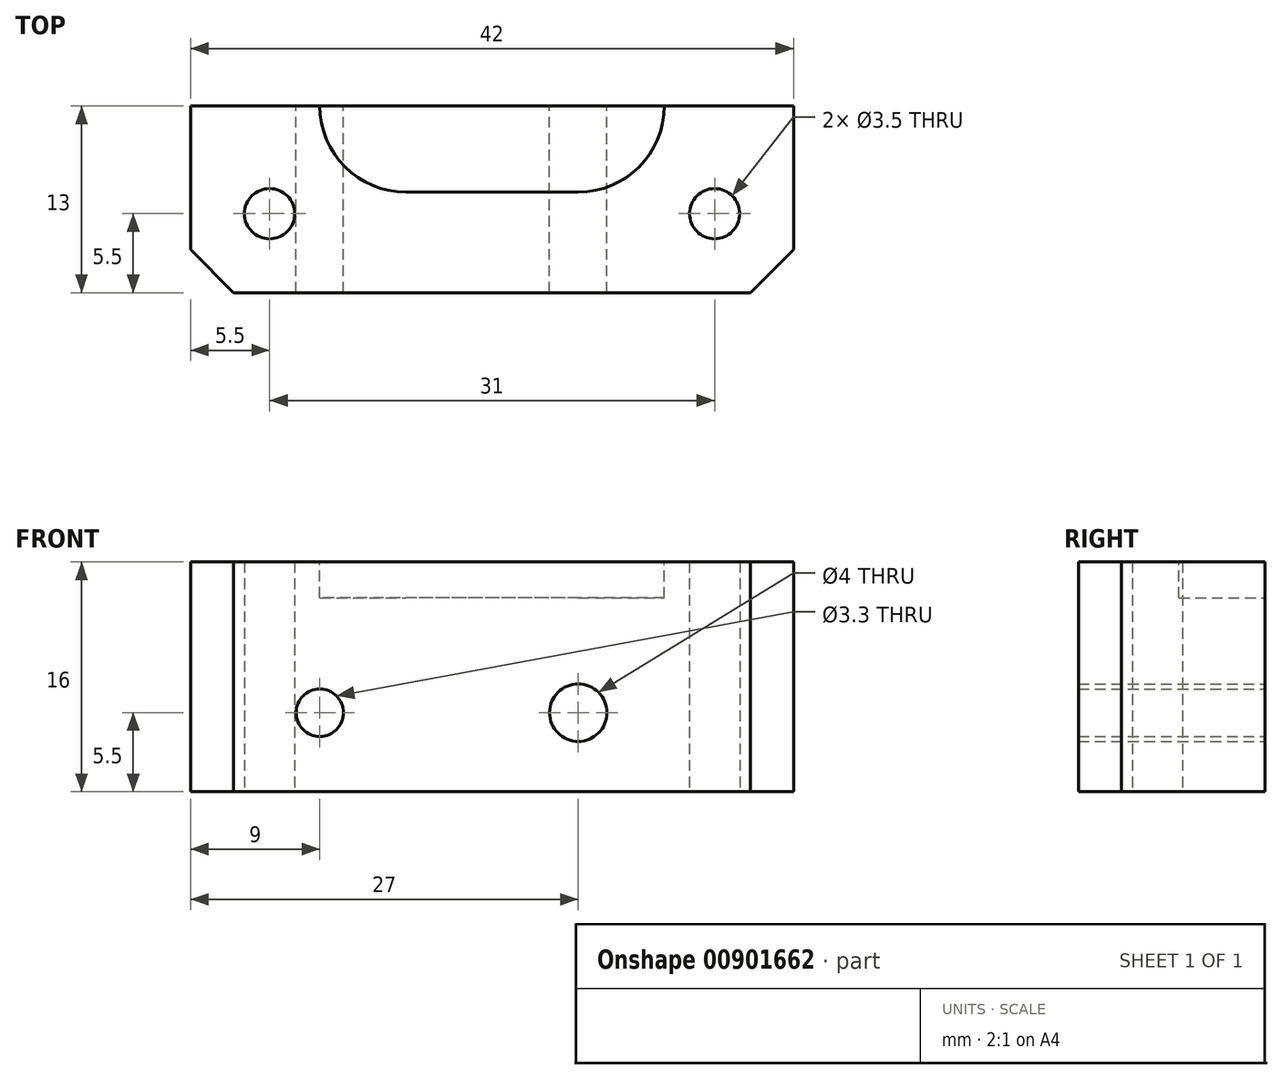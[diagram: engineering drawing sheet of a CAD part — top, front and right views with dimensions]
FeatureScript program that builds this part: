
annotation { "Feature Type Name" : "Feature", "Feature Type Description" : "" }
export const myFeature = defineFeature(function(context is Context, id is Id, definition is map)
    precondition{}
    {
        {
            var Q0;
            Q0=qCreatedBy(makeId("Top.planeOp"),FACE);
            var sketch = newSketch(context, id + "F0", { "sketchPlane" : qUnion([Q0])});
            skLineSegment(sketch, "E0.bottom", {"start": v(21, 6.5) * mm, "end": v(-21, 6.5) * mm});
            skLineSegment(sketch, "E0.top", {"start": v(21, -6.5) * mm, "end": v(-21, -6.5) * mm});
            skLineSegment(sketch, "E0.left", {"start": v(21, 6.5) * mm, "end": v(21, -6.5) * mm});
            skLineSegment(sketch, "E0.right", {"start": v(-21, 6.5) * mm, "end": v(-21, -6.5) * mm});
            skPoint(sketch, "E0.middle", {"position": v(0, 0) * mm});
            skCircle(sketch, "E1", {"center": v(-15.5, -1) * mm, "radius": 1.75 * mm});
            skLineSegment(sketch, "E2", {"start": v(0, 8.77) * mm, "end": v(0, -9.46) * mm, "construction": true});
            skPoint(sketch, "E2.endSnap0", {"position": v(0, 6.5) * mm});
            skCircle(sketch, "E3.MirrorC", {"center": v(15.5, -1) * mm, "radius": 1.75 * mm});
            skSolve(sketch);
        }
        {
            var Q0;
            Q0 = qSketchRegion(id + "F0", true);
            extrude(context, id + "F1", {"entities" : qUnion([Q0]), "endBound" : BoundingType.SYMMETRIC, "depth" : 16 * mm, "offsetDistance" : 25 * mm});
        }
        {
            var Q0;
            Q0=makeQuery(id+"F1.opExtrude","CAP_FACE",FACE,{"disambiguationData":[OSD([sQuery(id+"F0.wireOp",EDGE,"E0.bottom"),sQuery(id+"F0.wireOp",EDGE,"E0.top"),sQuery(id+"F0.wireOp",EDGE,"E0.left"),sQuery(id+"F0.wireOp",EDGE,"E0.right"),sQuery(id+"F0.wireOp",EDGE,"E1"),sQuery(id+"F0.wireOp",EDGE,"E3.MirrorC")])],"isStart":false});
            var sketch = newSketch(context, id + "F2", { "sketchPlane" : qUnion([Q0])});
            skLineSegment(sketch, "E4", {"start": v(0, 9.79) * mm, "end": v(0, -9.6) * mm, "construction": true});
            skLineSegment(sketch, "E5.bottom", {"start": v(12, 6.5) * mm, "end": v(-12, 6.5) * mm});
            skLineSegment(sketch, "E5.top", {"start": v(12, 0.5) * mm, "end": v(-12, 0.5) * mm});
            skLineSegment(sketch, "E5.left", {"start": v(12, 6.5) * mm, "end": v(12, 0.5) * mm});
            skLineSegment(sketch, "E5.right", {"start": v(-12, 6.5) * mm, "end": v(-12, 0.5) * mm});
            skPoint(sketch, "E5.middle", {"position": v(0, 3.5) * mm});
            skSolve(sketch);
        }
        {
            var Q0;
            Q0 = qSketchRegion(id + "F2", true);
            extrude(context, id + "F3", {"entities" : qUnion([Q0]), "operationType" : NewBodyOperationType.REMOVE, "oppositeDirection" : true, "depth" : 2.5 * mm, "offsetDistance" : 25 * mm});
        }
        {
            var Q0;
            Q0=makeQuery(id+"F3.boolean.opBoolean","COPY",EDGE,{"derivedFrom":makeQuery(id+"F3.opExtrude","SWEPT_EDGE",EDGE,{"disambiguationData":[OSD([sQuery(id+"F2.wireOp",EDGE,"E5.top"),sQuery(id+"F2.wireOp",EDGE,"E5.right")])]})});
            var Q1;
            Q1=makeQuery(id+"F3.boolean.opBoolean","COPY",EDGE,{"derivedFrom":makeQuery(id+"F3.opExtrude","SWEPT_EDGE",EDGE,{"disambiguationData":[OSD([sQuery(id+"F2.wireOp",EDGE,"E5.top"),sQuery(id+"F2.wireOp",EDGE,"E5.left")])]})});
            fillet(context, id + "F4", {"entities" : qUnion([Q0, Q1]), "radius" : 6 * mm, "tangentPropagation" : true, "allowEdgeOverflow" : false});
        }
        {
            var Q0;
            Q0=makeQuery(id+"F1.opExtrude","SWEPT_EDGE",EDGE,{"disambiguationData":[OSD([sQuery(id+"F0.wireOp",EDGE,"E0.top"),sQuery(id+"F0.wireOp",EDGE,"E0.right")])]});
            var Q1;
            Q1=makeQuery(id+"F1.opExtrude","SWEPT_EDGE",EDGE,{"disambiguationData":[OSD([sQuery(id+"F0.wireOp",EDGE,"E0.top"),sQuery(id+"F0.wireOp",EDGE,"E0.left")])]});
            chamfer(context, id + "F5", {"entities" : qUnion([Q0, Q1]), "width" : 3 * mm, "tangentPropagation" : true});
        }
        {
            var Q0;
            Q0=makeQuery(id+"F1.opExtrude","SWEPT_FACE",FACE,{"disambiguationData":[OSD([sQuery(id+"F0.wireOp",EDGE,"E0.bottom")])]});
            var sketch = newSketch(context, id + "F6", { "sketchPlane" : qUnion([Q0])});
            skCircle(sketch, "E6", {"center": v(12, -2.5) * mm, "radius": 1.65 * mm});
            skLineSegment(sketch, "E7", {"start": v(21, -2.5) * mm, "end": v(-21, -2.5) * mm, "construction": true});
            skCircle(sketch, "E8", {"center": v(-6, -2.5) * mm, "radius": 2 * mm});
            skSolve(sketch);
        }
        {
            var Q0;
            Q0 = qSketchRegion(id + "F6", true);
            extrude(context, id + "F7", {"entities" : qUnion([Q0]), "operationType" : NewBodyOperationType.REMOVE, "endBound" : BoundingType.THROUGH_ALL, "oppositeDirection" : true, "depth" : 25 * mm, "offsetDistance" : 25 * mm});
        }
    });
